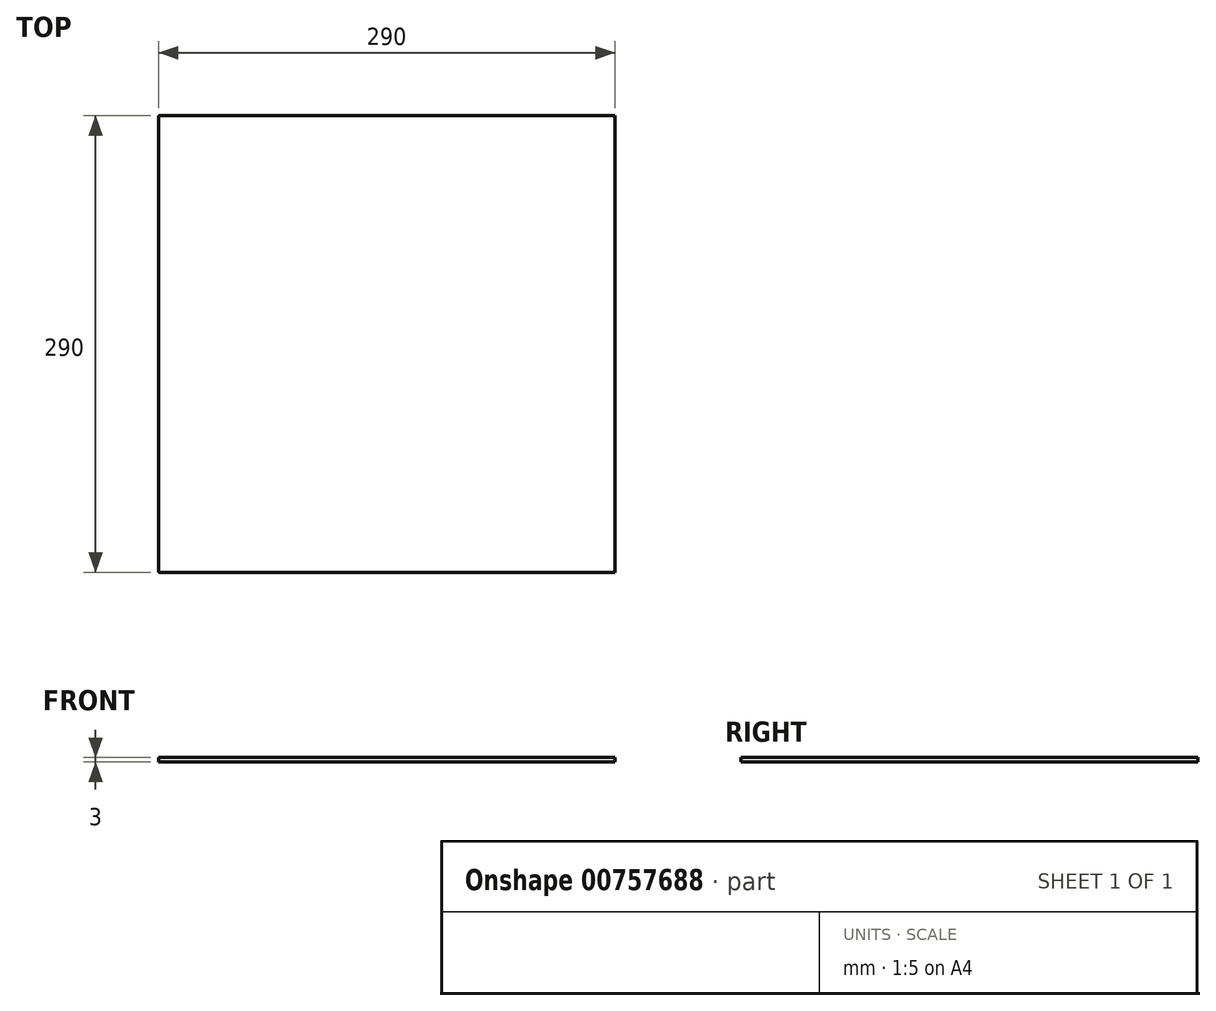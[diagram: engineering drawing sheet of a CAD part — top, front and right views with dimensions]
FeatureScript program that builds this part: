
annotation { "Feature Type Name" : "Feature", "Feature Type Description" : "" }
export const myFeature = defineFeature(function(context is Context, id is Id, definition is map)
    precondition{}
    {
        {
            var Q0;
            Q0=qCreatedBy(makeId("Top.planeOp"),FACE);
            var sketch = newSketch(context, id + "F0", { "sketchPlane" : qUnion([Q0])});
            skLineSegment(sketch, "E0.bottom", {"start": v(145, 145) * mm, "end": v(-145, 145) * mm});
            skLineSegment(sketch, "E0.top", {"start": v(145, -145) * mm, "end": v(-145, -145) * mm});
            skLineSegment(sketch, "E0.left", {"start": v(145, 145) * mm, "end": v(145, -145) * mm});
            skLineSegment(sketch, "E0.right", {"start": v(-145, 145) * mm, "end": v(-145, -145) * mm});
            skPoint(sketch, "E0.middle", {"position": v(0, 0) * mm});
            skSolve(sketch);
        }
        {
            var Q0;
            Q0=makeQuery(id+"F0.imprint","IMPRINT",FACE,{"disambiguationData":[TD([[makeQuery(id+"F0.imprint","IMPRINT",EDGE,{"derivedFrom":sQuery(id+"F0.wireOp",EDGE,"E0.bottom")}),1.0]])]});
            var Q1;
            Q1 = qSketchRegion(id + "F0", true);
            extrude(context, id + "F1", {"entities" : qUnion([Q0, Q1]), "depth" : 3 * mm, "offsetDistance" : 25 * mm});
        }
    });
